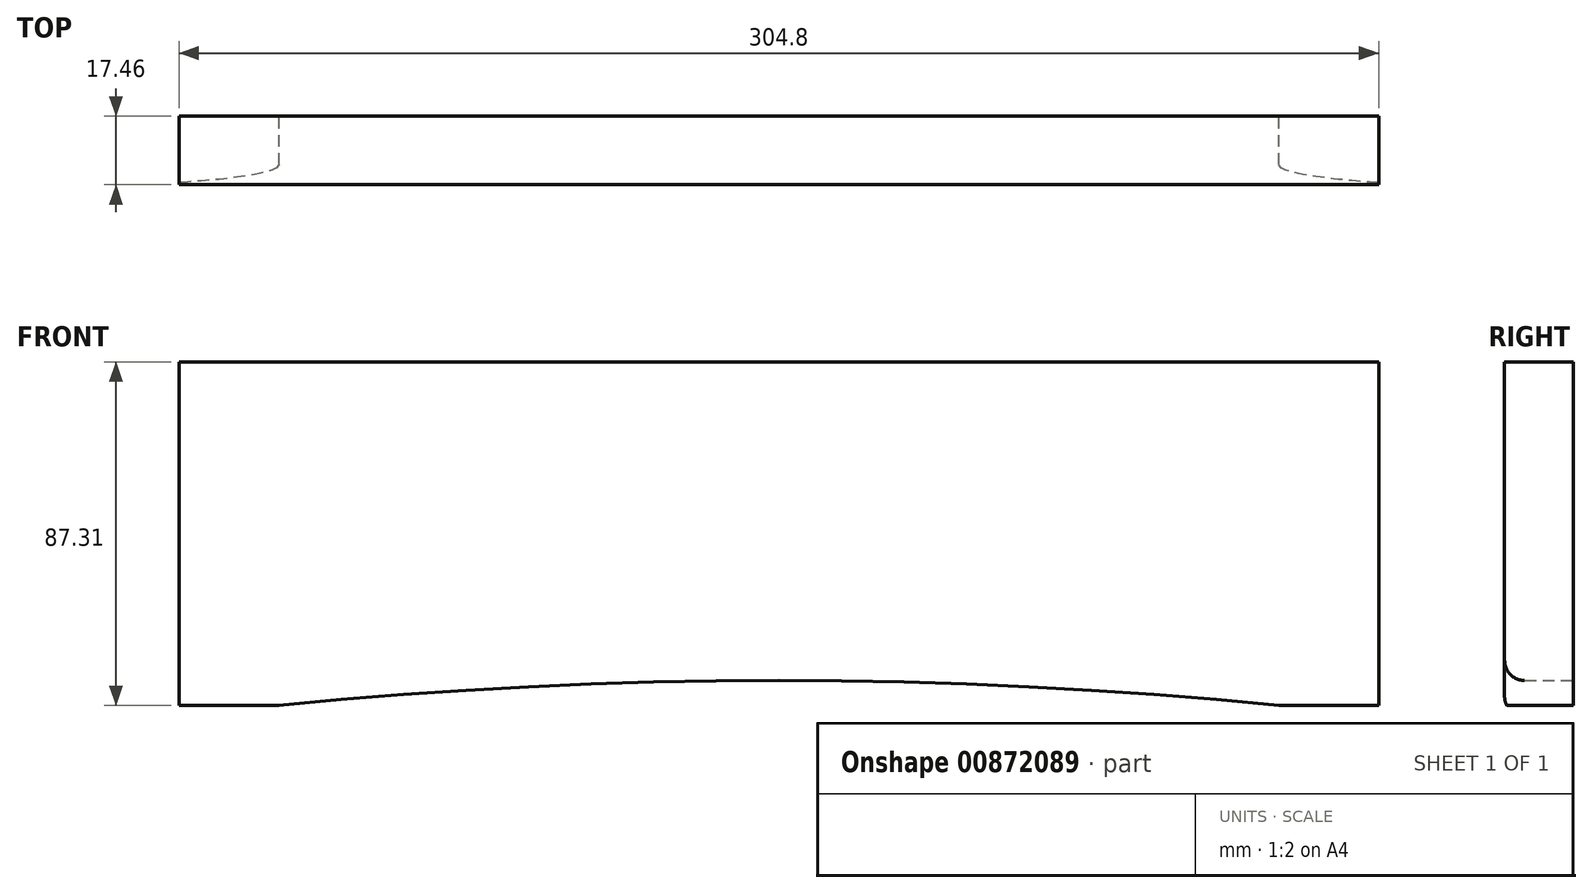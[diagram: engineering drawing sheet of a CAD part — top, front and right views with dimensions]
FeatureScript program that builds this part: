
annotation { "Feature Type Name" : "Feature", "Feature Type Description" : "" }
export const myFeature = defineFeature(function(context is Context, id is Id, definition is map)
    precondition{}
    {
        {
            var Q0;
            Q0=qCreatedBy(makeId("Front.planeOp"),FACE);
            var sketch = newSketch(context, id + "F0", { "sketchPlane" : qUnion([Q0])});
            skLineSegment(sketch, "E0.bottom", {"start": v(0, 0) * mm, "end": v(25.4, 0) * mm});
            skLineSegment(sketch, "E0.top", {"start": v(0, 87.31) * mm, "end": v(304.8, 87.31) * mm});
            skLineSegment(sketch, "E0.left", {"start": v(0, 0) * mm, "end": v(0, 87.31) * mm});
            skLineSegment(sketch, "E0.right", {"start": v(304.8, 0) * mm, "end": v(304.8, 87.31) * mm});
            skLineSegment(sketch, "E1", {"start": v(25.4, 19.19) * mm, "end": v(25.4, -27.7) * mm, "construction": true});
            skLineSegment(sketch, "E2", {"start": v(279.4, 17.97) * mm, "end": v(279.4, -25.26) * mm, "construction": true});
            skLineSegment(sketch, "E3", {"start": v(152.4, 6.35) * mm, "end": v(152.4, -24.04) * mm, "construction": true});
            skPoint(sketch, "E3.startSnap0", {"position": v(152.4, 0) * mm});
            skArc(sketch, "E4", {"start": v(279.4, 0) * mm, "mid": v(152.4, 6.35) * mm, "end": v(25.4, 0) * mm});
            skPoint(sketch, "E4.first.point", {"position": v(25.4, 0) * mm});
            skPoint(sketch, "E4.third.point", {"position": v(279.4, 0) * mm});
            skLineSegment(sketch, "E5.trimOffspring", {"start": v(279.4, 0) * mm, "end": v(304.8, 0) * mm});
            skSolve(sketch);
        }
        {
            var Q0;
            Q0=qSketchRegion(id+"F0",true);
            extrude(context, id + "F1", {"entities" : qUnion([Q0]), "depth" : 17.46 * mm});
        }
        {
            var Q0;
            Q0=makeQuery(id+"F1.opExtrude","CAP_EDGE",EDGE,{"disambiguationData":[OSD([sQuery(id+"F0.wireOp",EDGE,"E4")])],"isStart":false});
            fillet(context, id + "F2", {"entities" : qUnion([Q0]), "radius" : 5.08 * mm, "tangentPropagation" : true, "allowEdgeOverflow" : false});
        }
    });
